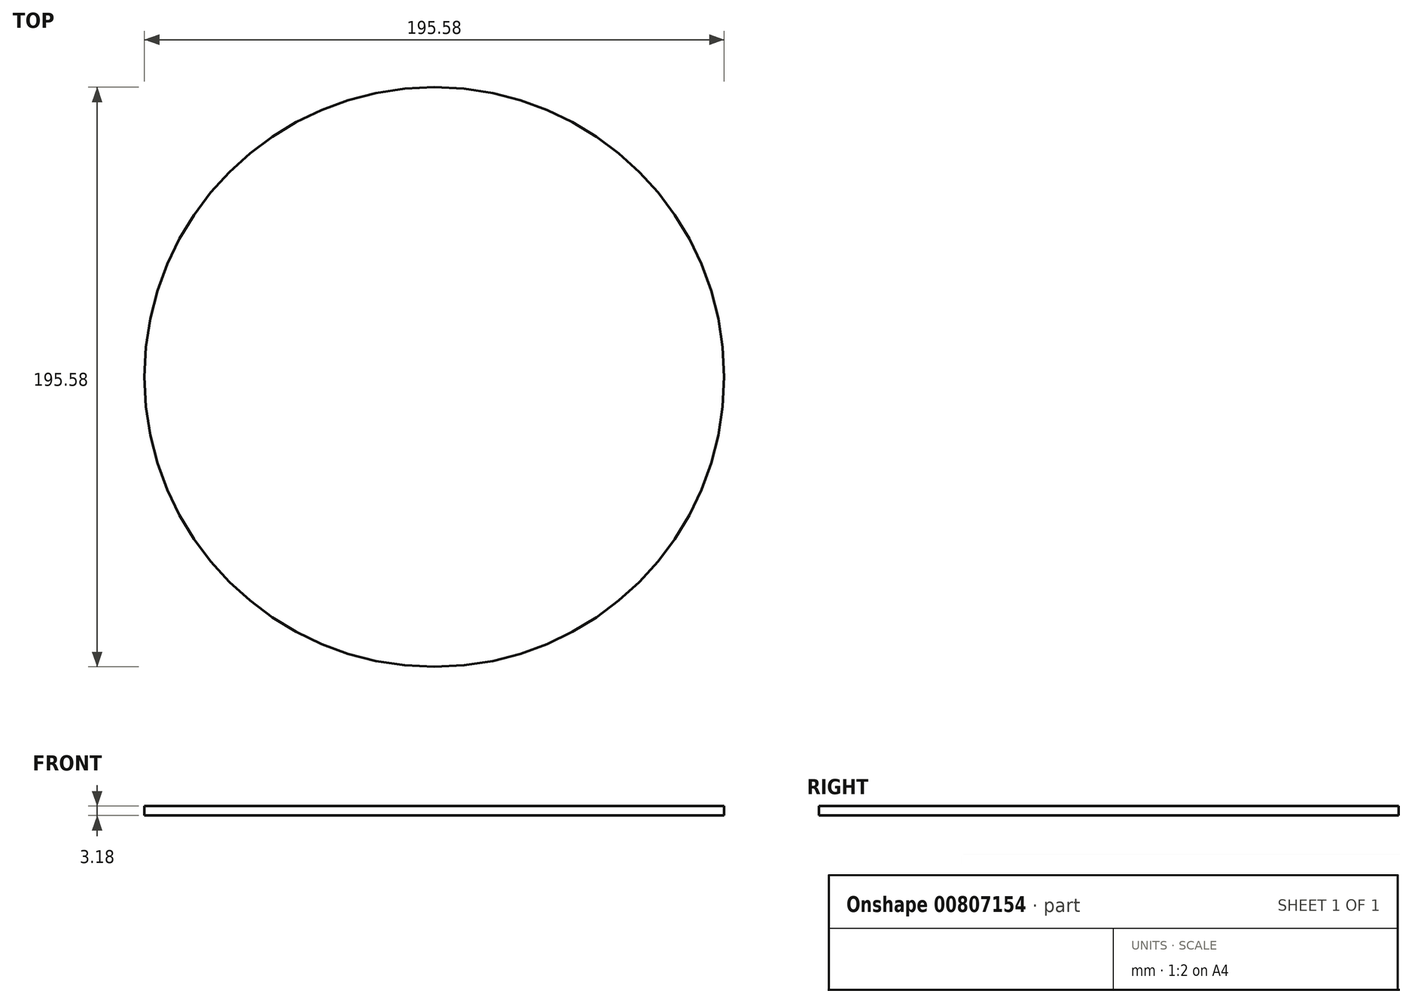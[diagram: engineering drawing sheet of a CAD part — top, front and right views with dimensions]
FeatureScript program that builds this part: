
annotation { "Feature Type Name" : "Feature", "Feature Type Description" : "" }
export const myFeature = defineFeature(function(context is Context, id is Id, definition is map)
    precondition{}
    {
        {
            var Q0;
            Q0=qCreatedBy(makeId("Top.planeOp"),FACE);
            var sketch = newSketch(context, id + "F0", { "sketchPlane" : qUnion([Q0])});
            skCircle(sketch, "E0", {"center": v(0, 0) * mm, "radius": 97.8 * mm});
            skSolve(sketch);
        }
        {
            var Q0;
            Q0=qSketchRegion(id+"F0",true);
            extrude(context, id + "F1", {"entities" : qUnion([Q0]), "depth" : 3.17 * mm, "offsetDistance" : 25.4 * mm});
        }
    });
